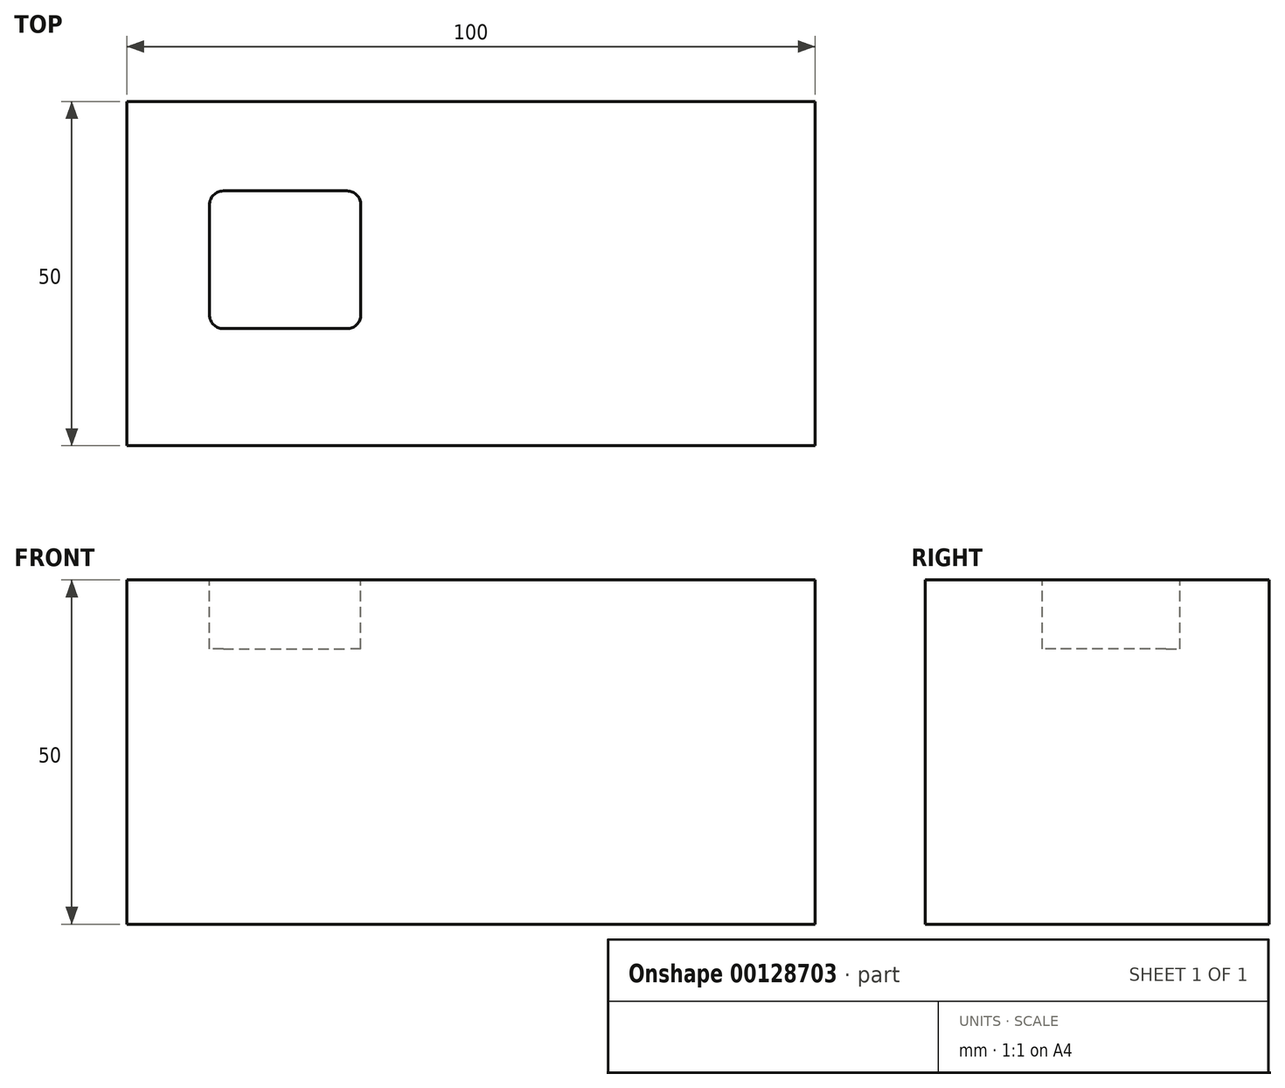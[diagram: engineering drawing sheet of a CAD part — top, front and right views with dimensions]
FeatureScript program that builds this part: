
annotation { "Feature Type Name" : "Feature", "Feature Type Description" : "" }
export const myFeature = defineFeature(function(context is Context, id is Id, definition is map)
    precondition{}
    {
        {
            var Q0;
            Q0=qCreatedBy(makeId("Top.planeOp"),FACE);
            var sketch = newSketch(context, id + "F0", { "sketchPlane" : qUnion([Q0])});
            skLineSegment(sketch, "E0.bottom", {"start": v(-50, 25) * mm, "end": v(50, 25) * mm});
            skLineSegment(sketch, "E0.top", {"start": v(-50, -25) * mm, "end": v(50, -25) * mm});
            skLineSegment(sketch, "E0.left", {"start": v(-50, 25) * mm, "end": v(-50, -25) * mm});
            skLineSegment(sketch, "E0.right", {"start": v(50, 25) * mm, "end": v(50, -25) * mm});
            skPoint(sketch, "E0.middle", {"position": v(0, 0) * mm});
            skSolve(sketch);
        }
        {
            var Q0;
            Q0=makeQuery(id+"F0.imprint","IMPRINT",FACE,{"disambiguationData":[TD([[makeQuery(id+"F0.imprint","IMPRINT",EDGE,{"derivedFrom":sQuery(id+"F0.wireOp",EDGE,"E0.bottom")}),-1.0]])]});
            extrude(context, id + "F1", {"entities" : qUnion([Q0]), "depth" : 50 * mm});
        }
        {
            var Q0;
            Q0=makeQuery(id+"F1.opExtrude","CAP_FACE",FACE,{"disambiguationData":[OSD([sQuery(id+"F0.wireOp",EDGE,"E0.bottom"),sQuery(id+"F0.wireOp",EDGE,"E0.top"),sQuery(id+"F0.wireOp",EDGE,"E0.left"),sQuery(id+"F0.wireOp",EDGE,"E0.right")])],"isStart":false});
            var sketch = newSketch(context, id + "F2", { "sketchPlane" : qUnion([Q0])});
            skLineSegment(sketch, "E1.bottom", {"start": v(-36, 12) * mm, "end": v(-18, 12) * mm});
            skLineSegment(sketch, "E1.top", {"start": v(-36, -8) * mm, "end": v(-18, -8) * mm});
            skLineSegment(sketch, "E1.left", {"start": v(-38, 10) * mm, "end": v(-38, -6) * mm});
            skLineSegment(sketch, "E1.right", {"start": v(-16, 10) * mm, "end": v(-16, -6) * mm});
            skPoint(sketch, "E2.visualSharp", {"position": v(-38, 12) * mm});
            skArc(sketch, "E2.filletArc", {"start": v(-36, 12) * mm, "mid": v(-37.41, 11.41) * mm, "end": v(-38, 10) * mm});
            skPoint(sketch, "E3.visualSharp", {"position": v(-16, 12) * mm});
            skArc(sketch, "E3.filletArc", {"start": v(-16, 10) * mm, "mid": v(-16.59, 11.41) * mm, "end": v(-18, 12) * mm});
            skPoint(sketch, "E4.visualSharp", {"position": v(-16, -8) * mm});
            skArc(sketch, "E4.filletArc", {"start": v(-18, -8) * mm, "mid": v(-16.59, -7.41) * mm, "end": v(-16, -6) * mm});
            skPoint(sketch, "E5.visualSharp", {"position": v(-38, -8) * mm});
            skArc(sketch, "E5.filletArc", {"start": v(-38, -6) * mm, "mid": v(-37.41, -7.41) * mm, "end": v(-36, -8) * mm});
            skSolve(sketch);
        }
        {
            var Q0;
            Q0=makeQuery(id+"F2.imprint","IMPRINT",FACE,{"disambiguationData":[TD([[makeQuery(id+"F2.imprint","IMPRINT",EDGE,{"derivedFrom":sQuery(id+"F2.wireOp",EDGE,"E1.bottom")}),-1.0]])]});
            extrude(context, id + "F3", {"entities" : qUnion([Q0]), "operationType" : NewBodyOperationType.REMOVE, "oppositeDirection" : true, "depth" : 10 * mm});
        }
    });
